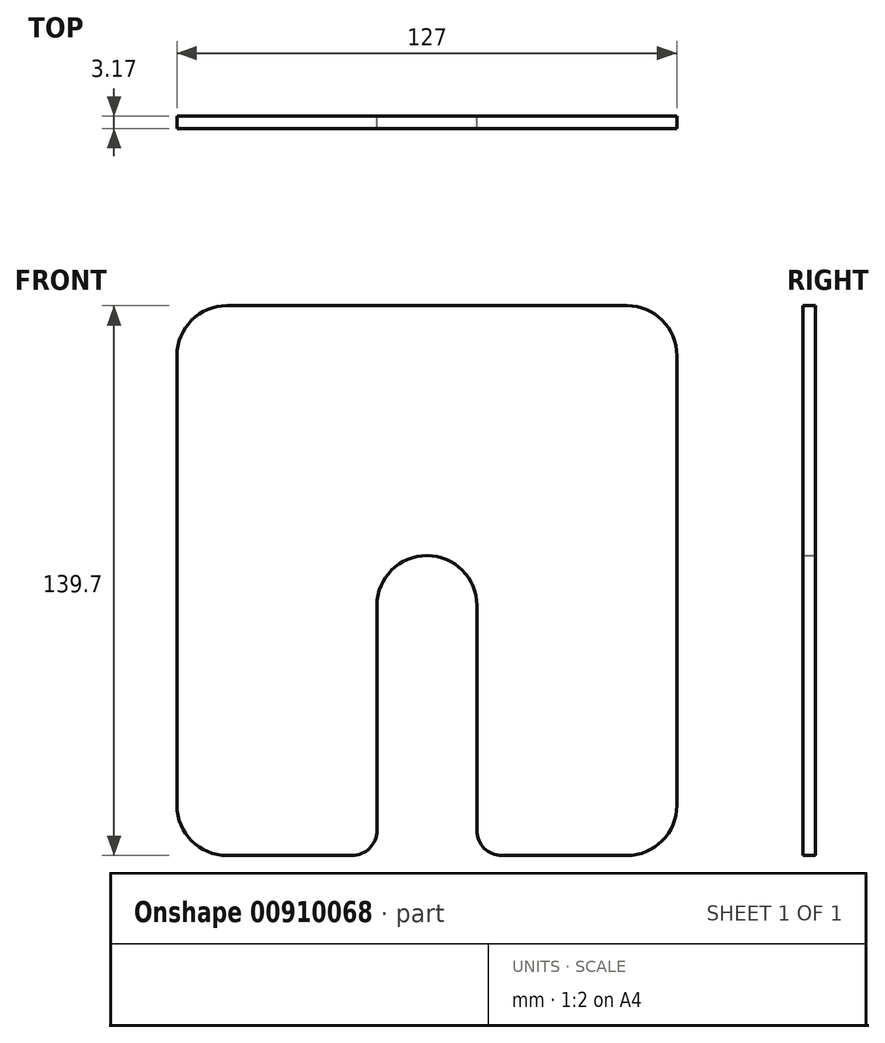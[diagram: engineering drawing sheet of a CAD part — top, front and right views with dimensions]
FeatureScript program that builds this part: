
annotation { "Feature Type Name" : "Feature", "Feature Type Description" : "" }
export const myFeature = defineFeature(function(context is Context, id is Id, definition is map)
    precondition{}
    {
        {
            var Q0;
            Q0=qCreatedBy(makeId("Front.planeOp"),FACE);
            var sketch = newSketch(context, id + "F0", { "sketchPlane" : qUnion([Q0])});
            skLineSegment(sketch, "E0.bottom", {"start": v(50.8, -63.5) * mm, "end": v(19.05, -63.5) * mm});
            skLineSegment(sketch, "E0.top", {"start": v(50.8, 76.2) * mm, "end": v(-50.8, 76.2) * mm});
            skLineSegment(sketch, "E0.left", {"start": v(63.5, -50.8) * mm, "end": v(63.5, 63.5) * mm});
            skLineSegment(sketch, "E0.right", {"start": v(-63.5, -50.8) * mm, "end": v(-63.5, 63.5) * mm});
            skPoint(sketch, "E0.middle", {"position": v(0, 0) * mm});
            skArc(sketch, "E1", {"start": v(12.7, 0) * mm, "mid": v(0, 12.7) * mm, "end": v(-12.7, 0) * mm});
            skLineSegment(sketch, "E2", {"start": v(-12.7, 0) * mm, "end": v(-12.7, -57.15) * mm});
            skLineSegment(sketch, "E3", {"start": v(12.7, 0) * mm, "end": v(12.7, -57.15) * mm});
            skLineSegment(sketch, "E4.trimOffspring", {"start": v(-19.05, -63.5) * mm, "end": v(-50.8, -63.5) * mm});
            skArc(sketch, "E5.filletArc", {"start": v(-63.5, -50.8) * mm, "mid": v(-59.78, -59.78) * mm, "end": v(-50.8, -63.5) * mm});
            skArc(sketch, "E6.filletArc", {"start": v(50.8, -63.5) * mm, "mid": v(59.78, -59.78) * mm, "end": v(63.5, -50.8) * mm});
            skArc(sketch, "E7.filletArc", {"start": v(-50.8, 76.2) * mm, "mid": v(-59.78, 72.48) * mm, "end": v(-63.5, 63.5) * mm});
            skArc(sketch, "E8.filletArc", {"start": v(63.5, 63.5) * mm, "mid": v(59.78, 72.48) * mm, "end": v(50.8, 76.2) * mm});
            skPoint(sketch, "E9.visualSharp", {"position": v(-12.7, -63.5) * mm});
            skArc(sketch, "E9.filletArc", {"start": v(-19.05, -63.5) * mm, "mid": v(-14.56, -61.64) * mm, "end": v(-12.7, -57.15) * mm});
            skPoint(sketch, "E10.visualSharp", {"position": v(12.7, -63.5) * mm});
            skArc(sketch, "E10.filletArc", {"start": v(12.7, -57.15) * mm, "mid": v(14.56, -61.64) * mm, "end": v(19.05, -63.5) * mm});
            skLineSegment(sketch, "E11", {"start": v(-50.8, 63.5) * mm, "end": v(50.8, -50.8) * mm, "construction": true});
            skSolve(sketch);
        }
        {
            var Q0;
            Q0 = qSketchRegion(id + "F0", true);
            extrude(context, id + "F1", {"entities" : qUnion([Q0]), "depth" : 3.17 * mm, "offsetDistance" : 25.4 * mm});
        }
    });
